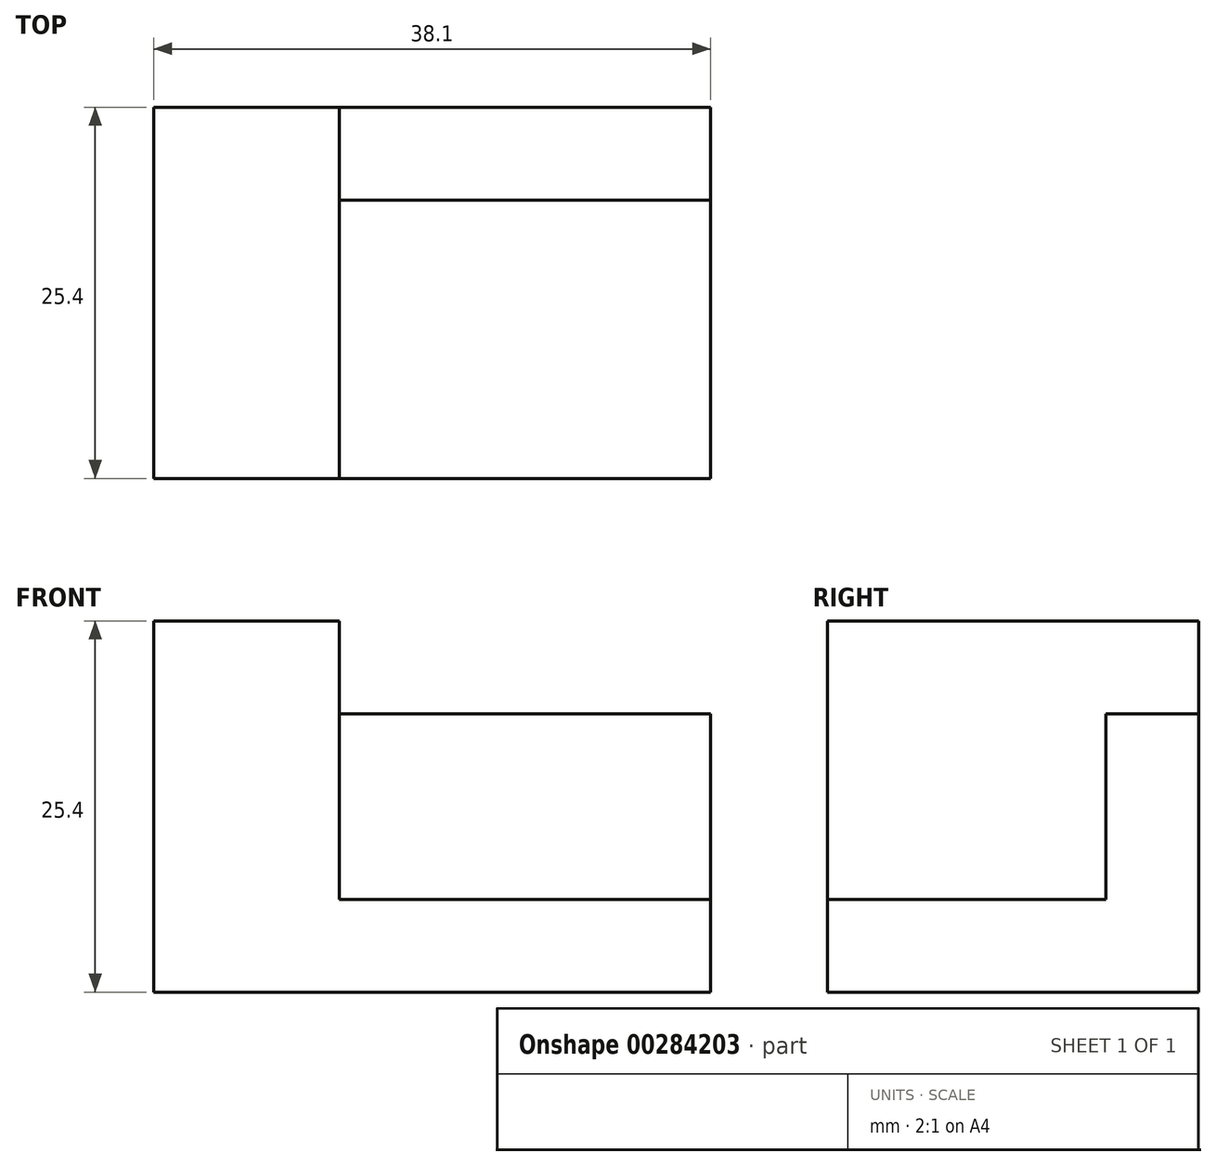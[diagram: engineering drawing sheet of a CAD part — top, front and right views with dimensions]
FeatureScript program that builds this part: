
annotation { "Feature Type Name" : "Feature", "Feature Type Description" : "" }
export const myFeature = defineFeature(function(context is Context, id is Id, definition is map)
    precondition{}
    {
        {
            var Q0;
            Q0=qCreatedBy(makeId("Front.planeOp"),FACE);
            var sketch = newSketch(context, id + "F0", { "sketchPlane" : qUnion([Q0])});
            skLineSegment(sketch, "E0.bottom", {"start": v(0, 0) * mm, "end": v(38.1, 0) * mm});
            skLineSegment(sketch, "E0.top", {"start": v(0, 25.4) * mm, "end": v(38.1, 25.4) * mm});
            skLineSegment(sketch, "E0.left", {"start": v(0, 0) * mm, "end": v(0, 25.4) * mm});
            skLineSegment(sketch, "E0.right", {"start": v(38.1, 0) * mm, "end": v(38.1, 25.4) * mm});
            skSolve(sketch);
        }
        {
            var Q0;
            Q0=makeQuery(id+"F0.imprint","IMPRINT",FACE,{"disambiguationData":[TD([[makeQuery(id+"F0.imprint","IMPRINT",EDGE,{"derivedFrom":sQuery(id+"F0.wireOp",EDGE,"E0.bottom")}),1.0]])]});
            extrude(context, id + "F1", {"entities" : qUnion([Q0]), "oppositeDirection" : true, "depth" : 25.4 * mm});
        }
        {
            var Q0;
            Q0=makeQuery(id+"F1.opExtrude","SWEPT_FACE",FACE,{"disambiguationData":[OSD([sQuery(id+"F0.wireOp",EDGE,"E0.right")])]});
            var sketch = newSketch(context, id + "F2", { "sketchPlane" : qUnion([Q0])});
            skLineSegment(sketch, "E1", {"start": v(25.4, 25.4) * mm, "end": v(0, 25.4) * mm});
            skLineSegment(sketch, "E2", {"start": v(0, 25.4) * mm, "end": v(0, 6.35) * mm});
            skLineSegment(sketch, "E3", {"start": v(0, 6.35) * mm, "end": v(19.05, 6.35) * mm});
            skLineSegment(sketch, "E4", {"start": v(19.05, 6.35) * mm, "end": v(19.05, 19.05) * mm});
            skLineSegment(sketch, "E5", {"start": v(19.05, 19.05) * mm, "end": v(25.4, 19.05) * mm});
            skLineSegment(sketch, "E6", {"start": v(25.4, 25.4) * mm, "end": v(25.4, 19.05) * mm});
            skSolve(sketch);
        }
        {
            var Q0;
            Q0 = qSketchRegion(id + "F2", true);
            extrude(context, id + "F3", {"entities" : qUnion([Q0]), "operationType" : NewBodyOperationType.REMOVE, "oppositeDirection" : true, "depth" : 25.4 * mm});
        }
    });
